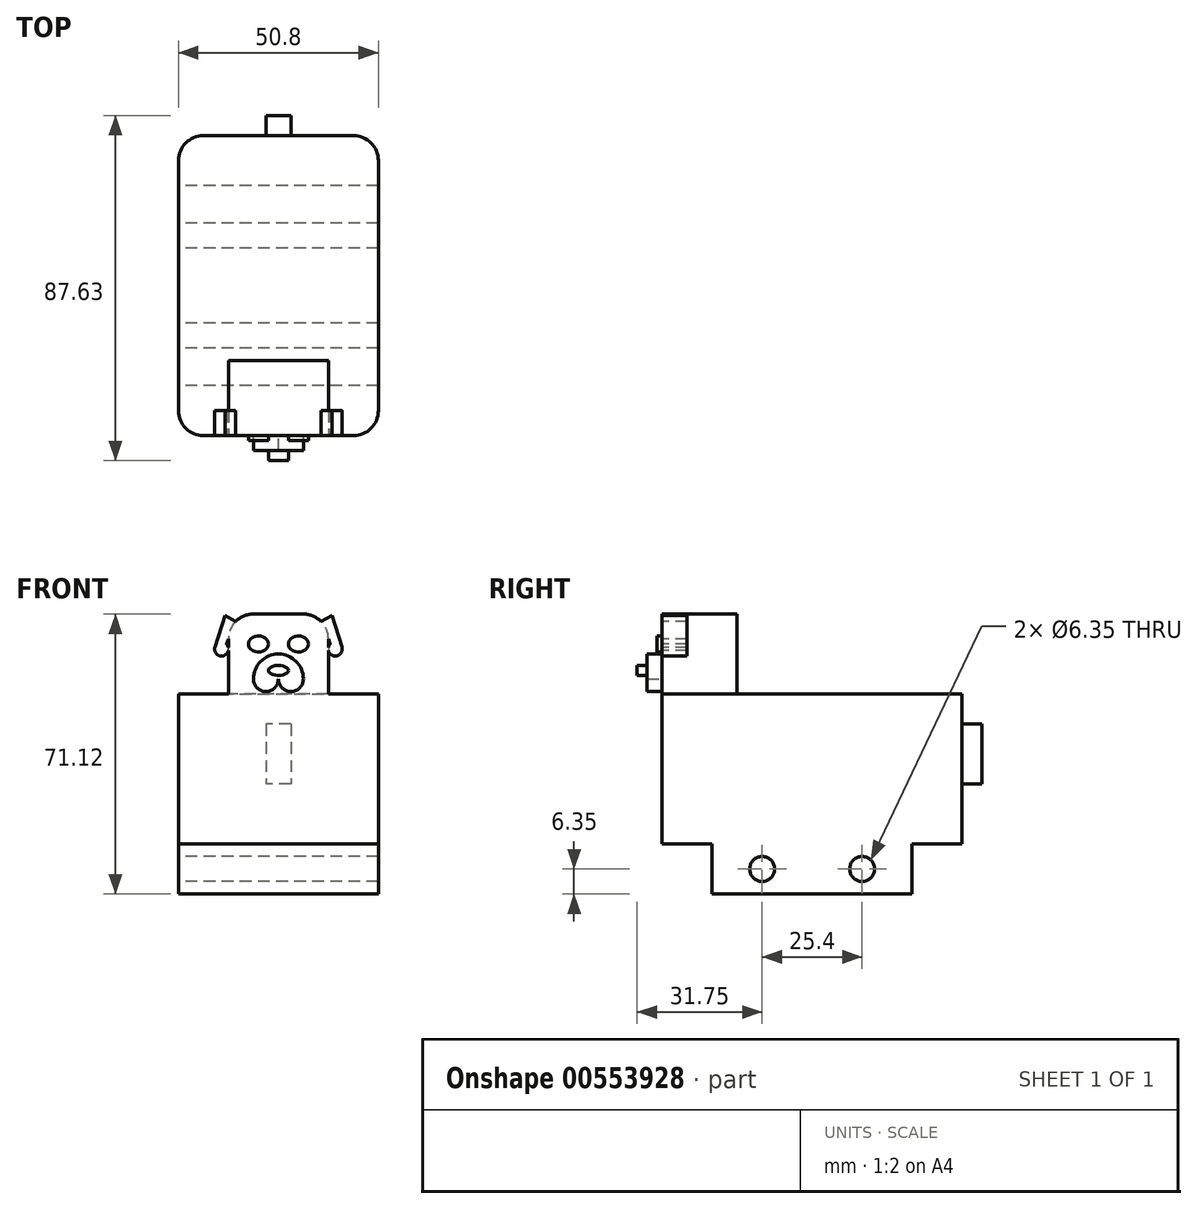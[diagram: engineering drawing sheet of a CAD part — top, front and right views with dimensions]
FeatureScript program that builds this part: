
annotation { "Feature Type Name" : "Feature", "Feature Type Description" : "" }
export const myFeature = defineFeature(function(context is Context, id is Id, definition is map)
    precondition{}
    {
        {
            var Q0;
            Q0=qCreatedBy(makeId("Top.planeOp"),FACE);
            var sketch = newSketch(context, id + "F0", { "sketchPlane" : qUnion([Q0])});
            skLineSegment(sketch, "E0", {"start": v(0, 6.35) * mm, "end": v(0, 69.85) * mm});
            skLineSegment(sketch, "E1", {"start": v(50.8, 69.85) * mm, "end": v(50.8, 6.35) * mm});
            skLineSegment(sketch, "E2", {"start": v(44.45, 0) * mm, "end": v(6.35, 0) * mm});
            skLineSegment(sketch, "E3", {"start": v(6.35, 76.2) * mm, "end": v(44.45, 76.2) * mm});
            skPoint(sketch, "E4.visualSharp", {"position": v(0, 76.2) * mm});
            skArc(sketch, "E4.filletArc", {"start": v(6.35, 76.2) * mm, "mid": v(1.86, 74.34) * mm, "end": v(0, 69.85) * mm});
            skPoint(sketch, "E5.visualSharp", {"position": v(50.8, 76.2) * mm});
            skArc(sketch, "E5.filletArc", {"start": v(50.8, 69.85) * mm, "mid": v(48.94, 74.34) * mm, "end": v(44.45, 76.2) * mm});
            skPoint(sketch, "E6.visualSharp", {"position": v(50.8, 0) * mm});
            skArc(sketch, "E6.filletArc", {"start": v(44.45, 0) * mm, "mid": v(48.94, 1.86) * mm, "end": v(50.8, 6.35) * mm});
            skPoint(sketch, "E7.visualSharp", {"position": v(0, 0) * mm});
            skArc(sketch, "E7.filletArc", {"start": v(0, 6.35) * mm, "mid": v(1.86, 1.86) * mm, "end": v(6.35, 0) * mm});
            skSolve(sketch);
        }
        {
            var Q0;
            Q0 = qSketchRegion(id + "F0", true);
            extrude(context, id + "F1", {"entities" : qUnion([Q0]), "depth" : 38.1 * mm, "offsetDistance" : 25.4 * mm});
        }
        {
            var Q0;
            Q0=makeQuery(id+"F1.opExtrude","CAP_FACE",FACE,{"disambiguationData":[OSD([sQuery(id+"F0.wireOp",EDGE,"E0"),sQuery(id+"F0.wireOp",EDGE,"E1"),sQuery(id+"F0.wireOp",EDGE,"E2"),sQuery(id+"F0.wireOp",EDGE,"E3")])],"isStart":true});
            var sketch = newSketch(context, id + "F2", { "sketchPlane" : qUnion([Q0])});
            skLineSegment(sketch, "E8.0", {"start": v(44.45, -69.85) * mm, "end": v(44.45, -6.35) * mm});
            skLineSegment(sketch, "E8.1", {"start": v(6.35, -69.85) * mm, "end": v(44.45, -69.85) * mm});
            skLineSegment(sketch, "E8.2", {"start": v(6.35, -6.35) * mm, "end": v(6.35, -69.85) * mm});
            skLineSegment(sketch, "E8.3", {"start": v(44.45, -6.35) * mm, "end": v(6.35, -6.35) * mm});
            skSolve(sketch);
        }
        {
            var Q0;
            Q0=makeQuery(id+"F1.opExtrude","SWEPT_FACE",FACE,{"disambiguationData":[OSD([sQuery(id+"F0.wireOp",EDGE,"E0")])]});
            var sketch = newSketch(context, id + "F3", { "sketchPlane" : qUnion([Q0])});
            skLineSegment(sketch, "E9", {"start": v(-63.5, 0) * mm, "end": v(-63.5, -12.7) * mm});
            skLineSegment(sketch, "E10", {"start": v(-63.5, -12.7) * mm, "end": v(-12.7, -12.7) * mm});
            skLineSegment(sketch, "E11", {"start": v(-12.7, -12.7) * mm, "end": v(-12.7, 0) * mm});
            skLineSegment(sketch, "E12", {"start": v(-38.1, 0) * mm, "end": v(-38.1, -12.7) * mm, "construction": true});
            skCircle(sketch, "E13", {"center": v(-50.8, -6.35) * mm, "radius": 3.18 * mm});
            skCircle(sketch, "E14", {"center": v(-25.4, -6.35) * mm, "radius": 3.18 * mm});
            skSolve(sketch);
        }
        {
            var Q0;
            {var subQ1=sQuery(id+"F3.wireOp",EDGE,"E9");Q0=makeQuery(id+"F3.imprint","IMPRINT",FACE,{"disambiguationData":[TD([[makeQuery(id+"F3.imprint","IMPRINT",EDGE,{"derivedFrom":subQ1}),1.0]])]});}
            var Q1;
            Q1=makeQuery(id+"F1.opExtrude","SWEPT_FACE",FACE,{"disambiguationData":[OSD([sQuery(id+"F0.wireOp",EDGE,"E1")])]});
            extrude(context, id + "F4", {"entities" : qUnion([Q0]), "operationType" : NewBodyOperationType.ADD, "endBound" : BoundingType.UP_TO_SURFACE, "oppositeDirection" : true, "depth" : 25.4 * mm, "endBoundEntityFace" : qUnion([Q1]), "offsetDistance" : 25.4 * mm});
        }
        {
            var Q0;
            Q0=makeQuery(id+"F1.opExtrude","SWEPT_FACE",FACE,{"disambiguationData":[OSD([sQuery(id+"F0.wireOp",EDGE,"E2")])]});
            var sketch = newSketch(context, id + "F5", { "sketchPlane" : qUnion([Q0])});
            skLineSegment(sketch, "E15", {"start": v(12.7, 38.1) * mm, "end": v(12.7, 52.07) * mm});
            skLineSegment(sketch, "E16", {"start": v(19.05, 58.42) * mm, "end": v(31.75, 58.42) * mm});
            skLineSegment(sketch, "E17", {"start": v(38.1, 52.07) * mm, "end": v(38.1, 38.1) * mm});
            skLineSegment(sketch, "E18.bottom", {"start": v(25.4, 48.26) * mm, "end": v(25.4, 48.26) * mm});
            skLineSegment(sketch, "E18.left", {"start": v(19.05, 41.91) * mm, "end": v(19.05, 41.91) * mm});
            skLineSegment(sketch, "E18.right", {"start": v(31.75, 41.91) * mm, "end": v(31.75, 41.9) * mm});
            skArc(sketch, "E19.filletArc", {"start": v(25.4, 48.26) * mm, "mid": v(20.9, 46.4) * mm, "end": v(19.05, 41.91) * mm});
            skArc(sketch, "E20.filletArc", {"start": v(31.75, 41.91) * mm, "mid": v(29.9, 46.4) * mm, "end": v(25.4, 48.26) * mm});
            skArc(sketch, "E21", {"start": v(19.05, 41.91) * mm, "mid": v(22.23, 38.74) * mm, "end": v(25.4, 41.91) * mm});
            skArc(sketch, "E22", {"start": v(25.4, 41.91) * mm, "mid": v(28.57, 38.74) * mm, "end": v(31.75, 41.91) * mm});
            skPoint(sketch, "E23.visualSharp", {"position": v(38.1, 58.42) * mm});
            skArc(sketch, "E23.filletArc", {"start": v(38.1, 52.07) * mm, "mid": v(36.24, 56.56) * mm, "end": v(31.75, 58.42) * mm});
            skPoint(sketch, "E24.visualSharp", {"position": v(12.7, 58.42) * mm});
            skArc(sketch, "E24.filletArc", {"start": v(19.05, 58.42) * mm, "mid": v(14.56, 56.56) * mm, "end": v(12.7, 52.07) * mm});
            skSolve(sketch);
        }
        {
            var Q0;
            {var subQ1=sQuery(id+"F5.wireOp",EDGE,"E15");Q0=makeQuery(id+"F5.imprint","IMPRINT",FACE,{"disambiguationData":[TD([[makeQuery(id+"F5.imprint","IMPRINT",EDGE,{"derivedFrom":subQ1}),-1.0]])]});}
            var Q1;
            Q1=makeQuery(id+"F5.imprint","IMPRINT",FACE,{"disambiguationData":[TD([[makeQuery(id+"F5.imprint","IMPRINT",EDGE,{"derivedFrom":sQuery(id+"F5.wireOp",EDGE,"E19.filletArc")}),1.0]])]});
            extrude(context, id + "F6", {"entities" : qUnion([Q0, Q1]), "operationType" : NewBodyOperationType.ADD, "oppositeDirection" : true, "depth" : 19.05 * mm, "offsetDistance" : 25.4 * mm});
        }
        {
            var Q0;
            Q0=makeQuery(id+"F5.imprint","IMPRINT",FACE,{"disambiguationData":[TD([[makeQuery(id+"F5.imprint","IMPRINT",EDGE,{"derivedFrom":sQuery(id+"F5.wireOp",EDGE,"E19.filletArc")}),1.0]])]});
            extrude(context, id + "F7", {"entities" : qUnion([Q0]), "operationType" : NewBodyOperationType.ADD, "depth" : 3.8 * mm, "offsetDistance" : 25.4 * mm});
        }
        {
            var Q0;
            Q0=makeQuery(id+"F7.opExtrude","CAP_FACE",FACE,{"disambiguationData":[OSD([sQuery(id+"F5.wireOp",EDGE,"E19.filletArc"),sQuery(id+"F5.wireOp",EDGE,"E20.filletArc"),sQuery(id+"F5.wireOp",EDGE,"E21"),sQuery(id+"F5.wireOp",EDGE,"E22")])],"isStart":false});
            var sketch = newSketch(context, id + "F8", { "sketchPlane" : qUnion([Q0])});
            skEllipse(sketch, "E25", {"center": v(25.4, 44.1) * mm, "majorRadius": 2.54 * mm, "minorRadius": 1.27 * mm, "majorAxis": v(1, 0)});
            skLineSegment(sketch, "E26", {"start": v(25.4, 41.91) * mm, "end": v(25.4, 48.26) * mm, "construction": true});
            skSolve(sketch);
        }
        {
            var Q0;
            Q0=makeQuery(id+"F8.imprint","IMPRINT",FACE,{"disambiguationData":[TD([[makeQuery(id+"F8.imprint","IMPRINT",EDGE,{"derivedFrom":sQuery(id+"F8.wireOp",EDGE,"E25")}),1.0]])]});
            extrude(context, id + "F9", {"entities" : qUnion([Q0]), "operationType" : NewBodyOperationType.ADD, "depth" : 2.54 * mm, "offsetDistance" : 25.4 * mm});
        }
        {
            var Q0;
            {var subQ0=sQuery(id+"F0.wireOp",EDGE,"E2");Q0=makeQuery(id+"F6.boolean.opBoolean","MERGE",FACE,{"derivedFrom":[makeQuery(id+"F1.opExtrude","SWEPT_FACE",FACE,{"disambiguationData":[OSD([subQ0])]}),makeQuery(id+"F6.opExtrude","CAP_FACE",FACE,{"disambiguationData":[OSD([subQ0,sQuery(id+"F5.wireOp",EDGE,"E15"),sQuery(id+"F5.wireOp",EDGE,"E16"),sQuery(id+"F5.wireOp",EDGE,"E17")])],"isStart":true})]});}
            var sketch = newSketch(context, id + "F10", { "sketchPlane" : qUnion([Q0])});
            skLineSegment(sketch, "E27", {"start": v(12.7, 50.8) * mm, "end": v(38.1, 50.8) * mm});
            skEllipse(sketch, "E28", {"center": v(20.32, 50.8) * mm, "majorRadius": 2.54 * mm, "minorRadius": 2.03 * mm, "majorAxis": v(1, 0)});
            skEllipse(sketch, "E29", {"center": v(30.48, 50.8) * mm, "majorRadius": 2.54 * mm, "minorRadius": 2.03 * mm, "majorAxis": v(1, 0)});
            skLineSegment(sketch, "E30", {"start": v(11.8, 58.07) * mm, "end": v(9.27, 50.07) * mm});
            skArc(sketch, "E31", {"start": v(9.27, 50.07) * mm, "mid": v(11.39, 47.81) * mm, "end": v(12.21, 50.8) * mm});
            skLineSegment(sketch, "E32", {"start": v(12.7, 52.07) * mm, "end": v(12.21, 50.8) * mm});
            skLineSegment(sketch, "E33", {"start": v(14.56, 56.56) * mm, "end": v(11.8, 58.07) * mm});
            skLineSegment(sketch, "E34", {"start": v(25.4, 48.26) * mm, "end": v(25.4, 58.42) * mm, "construction": true});
            skArc(sketch, "E35.MirrorCS", {"start": v(41.53, 50.07) * mm, "mid": v(39.41, 47.81) * mm, "end": v(38.59, 50.8) * mm});
            skLineSegment(sketch, "E36.MirrorCS", {"start": v(38.1, 52.07) * mm, "end": v(38.59, 50.8) * mm});
            skLineSegment(sketch, "E37.MirrorCS", {"start": v(36.24, 56.56) * mm, "end": v(39, 58.07) * mm});
            skLineSegment(sketch, "E38.MirrorCS", {"start": v(39, 58.07) * mm, "end": v(41.53, 50.07) * mm});
            skSolve(sketch);
        }
        {
            var Q0;
            {var subQ0=sQuery(id+"F10.wireOp",EDGE,"E28");var subQ1=sQuery(id+"F10.wireOp",EDGE,"E27");var subQ2=makeQuery(id+"F10.imprint","INTERSECT",VERTEX,{"disambiguationData":[OD(0.0)],"derivedFrom":[subQ1,subQ0]});Q0=makeQuery(id+"F10.imprint","IMPRINT",FACE,{"disambiguationData":[TD([[makeQuery(id+"F10.imprint","IMPRINT",EDGE,{"disambiguationData":[TD([[subQ2,-1.0]])],"derivedFrom":subQ1}),1.0]])]});}
            var Q1;
            {var subQ0=sQuery(id+"F10.wireOp",EDGE,"E28");var subQ1=sQuery(id+"F10.wireOp",EDGE,"E27");var subQ2=makeQuery(id+"F10.imprint","INTERSECT",VERTEX,{"disambiguationData":[OD(0.0)],"derivedFrom":[subQ1,subQ0]});Q1=makeQuery(id+"F10.imprint","IMPRINT",FACE,{"disambiguationData":[TD([[makeQuery(id+"F10.imprint","IMPRINT",EDGE,{"disambiguationData":[TD([[subQ2,-1.0]])],"derivedFrom":subQ1}),-1.0]])]});}
            var Q2;
            {var subQ0=sQuery(id+"F10.wireOp",EDGE,"E29");var subQ1=sQuery(id+"F10.wireOp",EDGE,"E27");var subQ2=makeQuery(id+"F10.imprint","INTERSECT",VERTEX,{"disambiguationData":[OD(0.0)],"derivedFrom":[subQ1,subQ0]});Q2=makeQuery(id+"F10.imprint","IMPRINT",FACE,{"disambiguationData":[TD([[makeQuery(id+"F10.imprint","IMPRINT",EDGE,{"disambiguationData":[TD([[subQ2,-1.0]])],"derivedFrom":subQ1}),-1.0]])]});}
            var Q3;
            {var subQ0=sQuery(id+"F10.wireOp",EDGE,"E29");var subQ1=sQuery(id+"F10.wireOp",EDGE,"E27");var subQ2=makeQuery(id+"F10.imprint","INTERSECT",VERTEX,{"disambiguationData":[OD(0.0)],"derivedFrom":[subQ1,subQ0]});Q3=makeQuery(id+"F10.imprint","IMPRINT",FACE,{"disambiguationData":[TD([[makeQuery(id+"F10.imprint","IMPRINT",EDGE,{"disambiguationData":[TD([[subQ2,-1.0]])],"derivedFrom":subQ1}),1.0]])]});}
            var Q4;
            {var subQ1=sQuery(id+"F10.wireOp",EDGE,"E36.MirrorCS");Q4=makeQuery(id+"F10.imprint","IMPRINT",FACE,{"disambiguationData":[TD([[makeQuery(id+"F10.imprint","IMPRINT",EDGE,{"derivedFrom":subQ1}),1.0]])]});}
            var Q5;
            {var subQ4=sQuery(id+"F10.wireOp",EDGE,"E30");Q5=makeQuery(id+"F10.imprint","IMPRINT",FACE,{"disambiguationData":[TD([[makeQuery(id+"F10.imprint","IMPRINT",EDGE,{"derivedFrom":subQ4}),1.0]])]});}
            extrude(context, id + "F11", {"entities" : qUnion([Q0, Q1, Q2, Q3, Q4, Q5]), "operationType" : NewBodyOperationType.ADD, "oppositeDirection" : true, "depth" : 6.35 * mm, "offsetDistance" : 25.4 * mm});
        }
        {
            var Q0;
            {var subQ0=sQuery(id+"F10.wireOp",EDGE,"E28");var subQ1=sQuery(id+"F10.wireOp",EDGE,"E27");var subQ2=makeQuery(id+"F10.imprint","INTERSECT",VERTEX,{"disambiguationData":[OD(0.0)],"derivedFrom":[subQ1,subQ0]});Q0=makeQuery(id+"F10.imprint","IMPRINT",FACE,{"disambiguationData":[TD([[makeQuery(id+"F10.imprint","IMPRINT",EDGE,{"disambiguationData":[TD([[subQ2,-1.0]])],"derivedFrom":subQ1}),1.0]])]});}
            var Q1;
            {var subQ0=sQuery(id+"F10.wireOp",EDGE,"E28");var subQ1=sQuery(id+"F10.wireOp",EDGE,"E27");var subQ2=makeQuery(id+"F10.imprint","INTERSECT",VERTEX,{"disambiguationData":[OD(0.0)],"derivedFrom":[subQ1,subQ0]});Q1=makeQuery(id+"F10.imprint","IMPRINT",FACE,{"disambiguationData":[TD([[makeQuery(id+"F10.imprint","IMPRINT",EDGE,{"disambiguationData":[TD([[subQ2,-1.0]])],"derivedFrom":subQ1}),-1.0]])]});}
            var Q2;
            {var subQ0=sQuery(id+"F10.wireOp",EDGE,"E29");var subQ1=sQuery(id+"F10.wireOp",EDGE,"E27");var subQ2=makeQuery(id+"F10.imprint","INTERSECT",VERTEX,{"disambiguationData":[OD(0.0)],"derivedFrom":[subQ1,subQ0]});Q2=makeQuery(id+"F10.imprint","IMPRINT",FACE,{"disambiguationData":[TD([[makeQuery(id+"F10.imprint","IMPRINT",EDGE,{"disambiguationData":[TD([[subQ2,-1.0]])],"derivedFrom":subQ1}),1.0]])]});}
            var Q3;
            {var subQ0=sQuery(id+"F10.wireOp",EDGE,"E29");var subQ1=sQuery(id+"F10.wireOp",EDGE,"E27");var subQ2=makeQuery(id+"F10.imprint","INTERSECT",VERTEX,{"disambiguationData":[OD(0.0)],"derivedFrom":[subQ1,subQ0]});Q3=makeQuery(id+"F10.imprint","IMPRINT",FACE,{"disambiguationData":[TD([[makeQuery(id+"F10.imprint","IMPRINT",EDGE,{"disambiguationData":[TD([[subQ2,-1.0]])],"derivedFrom":subQ1}),-1.0]])]});}
            extrude(context, id + "F12", {"entities" : qUnion([Q0, Q1, Q2, Q3]), "operationType" : NewBodyOperationType.ADD, "depth" : 1.27 * mm, "offsetDistance" : 25.4 * mm});
        }
        {
            var Q0;
            Q0=makeQuery(id+"F1.opExtrude","SWEPT_FACE",FACE,{"disambiguationData":[OSD([sQuery(id+"F0.wireOp",EDGE,"E3")])]});
            var sketch = newSketch(context, id + "F13", { "sketchPlane" : qUnion([Q0])});
            skLineSegment(sketch, "E39.bottom", {"start": v(-28.58, 30.48) * mm, "end": v(-22.23, 30.48) * mm});
            skLineSegment(sketch, "E39.top", {"start": v(-28.58, 15.24) * mm, "end": v(-22.23, 15.24) * mm});
            skLineSegment(sketch, "E39.left", {"start": v(-28.58, 30.48) * mm, "end": v(-28.58, 15.24) * mm});
            skLineSegment(sketch, "E39.right", {"start": v(-22.23, 30.48) * mm, "end": v(-22.23, 15.24) * mm});
            skSolve(sketch);
        }
        {
            var Q0;
            Q0=makeQuery(id+"F13.imprint","IMPRINT",FACE,{"disambiguationData":[TD([[makeQuery(id+"F13.imprint","IMPRINT",EDGE,{"derivedFrom":sQuery(id+"F13.wireOp",EDGE,"E39.bottom")}),-1.0]])]});
            extrude(context, id + "F14", {"entities" : qUnion([Q0]), "operationType" : NewBodyOperationType.ADD, "depth" : 5.08 * mm, "offsetDistance" : 25.4 * mm});
        }
    });
